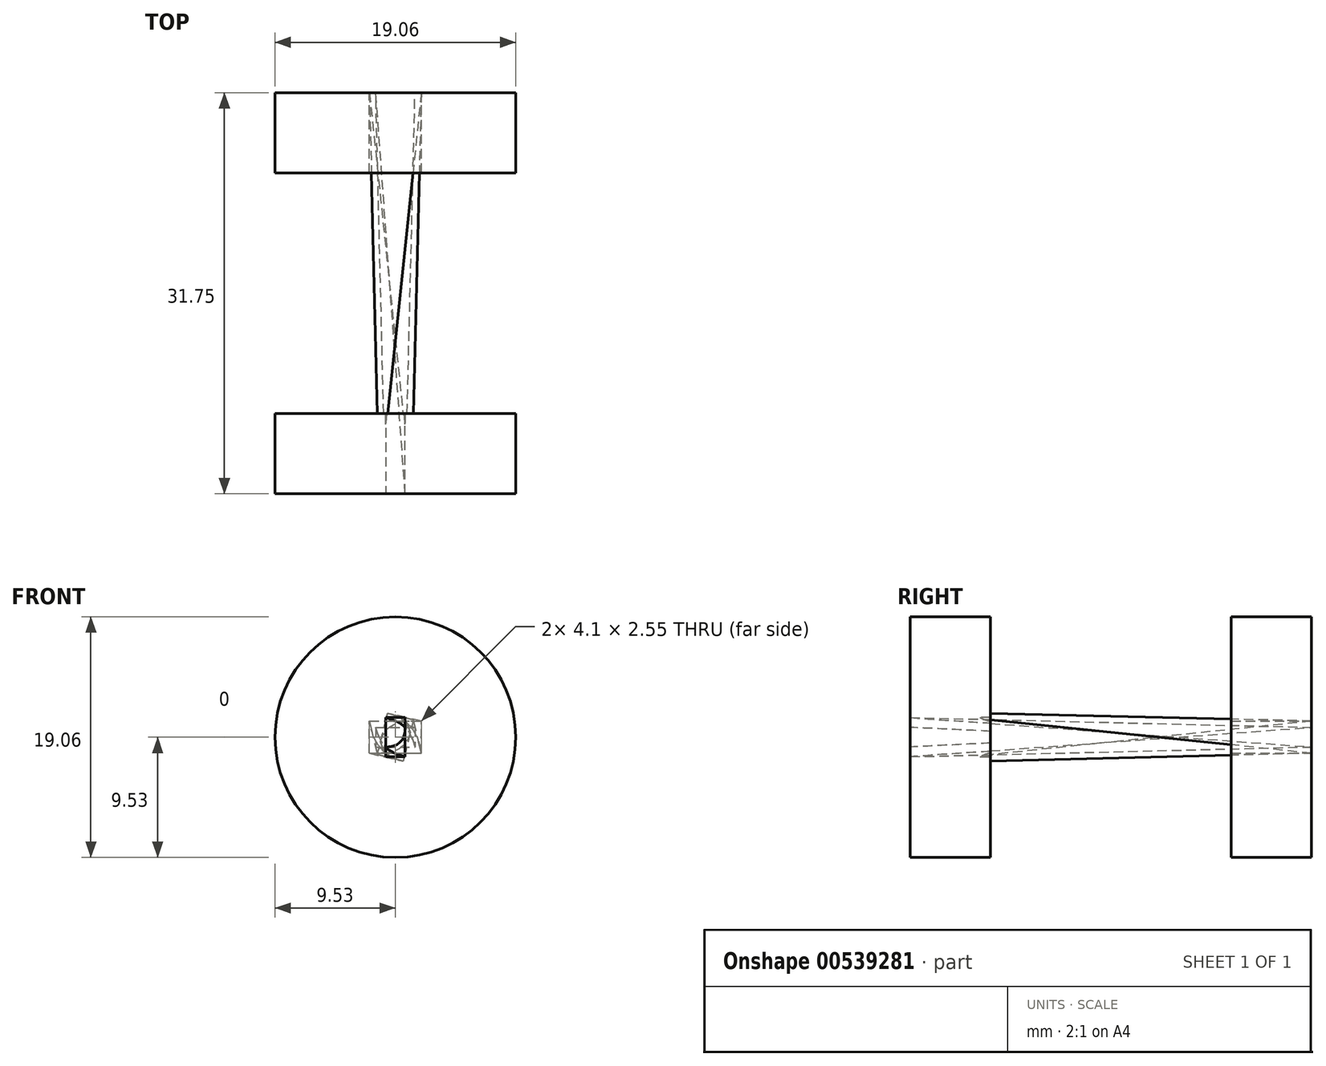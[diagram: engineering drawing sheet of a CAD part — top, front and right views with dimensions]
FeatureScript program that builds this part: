
annotation { "Feature Type Name" : "Feature", "Feature Type Description" : "" }
export const myFeature = defineFeature(function(context is Context, id is Id, definition is map)
    precondition{}
    {
        {
            var Q0;
            Q0=qCreatedBy(makeId("Front.planeOp"),FACE);
            var sketch = newSketch(context, id + "F0", { "sketchPlane" : qUnion([Q0])});
            skPoint(sketch, "E0.middle", {"position": v(0, 0) * mm});
            skLineSegment(sketch, "E1.bottom", {"start": v(-2.05, -1.27) * mm, "end": v(2.05, -1.27) * mm});
            skLineSegment(sketch, "E1.top", {"start": v(-2.05, 1.27) * mm, "end": v(2.05, 1.27) * mm});
            skLineSegment(sketch, "E1.left", {"start": v(-2.05, -1.27) * mm, "end": v(-2.05, 1.27) * mm});
            skLineSegment(sketch, "E1.right", {"start": v(2.05, -1.27) * mm, "end": v(2.05, 1.27) * mm});
            skCircle(sketch, "E2", {"center": v(0, 0) * mm, "radius": 9.53 * mm});
            skSolve(sketch);
        }
        {
            var Q0;
            Q0=qCreatedBy(makeId("Front.planeOp"),FACE);
            cPlane(context, id + "F1", {"entities" : qUnion([Q0]), "cplaneType" : CPlaneType.OFFSET, "offset" : 31.75 * mm, "width" : 150 * mm, "height" : 150 * mm});
        }
        {
            var Q0;
            Q0=qCreatedBy(id+"F1.planeOp",FACE);
            var sketch = newSketch(context, id + "F2", { "sketchPlane" : qUnion([Q0])});
            skLineSegment(sketch, "E3.bottom", {"start": v(-1.27, 2.05) * mm, "end": v(1.28, 2.05) * mm});
            skLineSegment(sketch, "E3.top", {"start": v(-1.28, -2.05) * mm, "end": v(1.27, -2.05) * mm});
            skLineSegment(sketch, "E3.left", {"start": v(-1.27, 2.05) * mm, "end": v(-1.28, -2.05) * mm});
            skLineSegment(sketch, "E3.right", {"start": v(1.28, 2.05) * mm, "end": v(1.27, -2.05) * mm});
            skPoint(sketch, "E3.middle", {"position": v(0, 0) * mm});
            skSolve(sketch);
        }
        {
            var Q0;
            Q0=qCreatedBy(id+"F1.planeOp",FACE);
            var sketch = newSketch(context, id + "F3", { "sketchPlane" : qUnion([Q0])});
            skLineSegment(sketch, "E4.bottom", {"start": v(-0.77, -1.55) * mm, "end": v(0.77, -1.55) * mm});
            skLineSegment(sketch, "E4.top", {"start": v(-0.78, 1.55) * mm, "end": v(0.77, 1.55) * mm});
            skLineSegment(sketch, "E4.left", {"start": v(-0.78, -1.55) * mm, "end": v(-0.78, 1.55) * mm});
            skLineSegment(sketch, "E4.right", {"start": v(0.78, -1.55) * mm, "end": v(0.77, 1.55) * mm});
            skPoint(sketch, "E4.middle", {"position": v(0, 0) * mm});
            skCircle(sketch, "E5", {"center": v(0, 0) * mm, "radius": 9.53 * mm});
            skSolve(sketch);
        }
        {
            var Q0;
            Q0=qCreatedBy(makeId("Front.planeOp"),FACE);
            var sketch = newSketch(context, id + "F4", { "sketchPlane" : qUnion([Q0])});
            skLineSegment(sketch, "E6.bottom", {"start": v(-1.55, 0.78) * mm, "end": v(1.55, 0.78) * mm});
            skLineSegment(sketch, "E6.top", {"start": v(-1.55, -0.78) * mm, "end": v(1.55, -0.78) * mm});
            skLineSegment(sketch, "E6.left", {"start": v(-1.55, 0.78) * mm, "end": v(-1.55, -0.78) * mm});
            skLineSegment(sketch, "E6.right", {"start": v(1.55, 0.78) * mm, "end": v(1.55, -0.78) * mm});
            skPoint(sketch, "E6.middle", {"position": v(0, 0) * mm});
            skSolve(sketch);
        }
        {
            var Q0;
            Q0=makeQuery(id+"F0.imprint","IMPRINT",FACE,{"disambiguationData":[TD([[makeQuery(id+"F0.imprint","IMPRINT",EDGE,{"derivedFrom":sQuery(id+"F0.wireOp",EDGE,"E1.bottom")}),-1.0]])]});
            extrude(context, id + "F5", {"entities" : qUnion([Q0]), "depth" : 6.35 * mm, "offsetDistance" : 25 * mm});
        }
        {
            var Q0;
            Q0=makeQuery(id+"F0.imprint","IMPRINT",FACE,{"disambiguationData":[TD([[makeQuery(id+"F0.imprint","IMPRINT",EDGE,{"derivedFrom":sQuery(id+"F0.wireOp",EDGE,"E1.bottom")}),1.0]])]});
            var Q1;
            Q1 = qSketchRegion(id + "F2", true);
            var Q2;
            Q2=sQuery(id+"F2.wireOp",VERTEX,"E3.right.start");
            var Q3;
            Q3=sQuery(id+"F0.wireOp",VERTEX,"E1.right.start");
            loft(context, id + "F6", {"sheetProfilesArray" : [{ "sheetProfileEntities" : qUnion([Q0]) }, { "sheetProfileEntities" : qUnion([Q1]) }], "matchConnections" : true, "connections" : [{ "connectionEntities" : qUnion([Q2, Q3]), "connectionEdgeQueries" : qUnion([]), "connectionEdgeParameters" : [] }]});
        }
        {
            var Q0;
            Q0=makeQuery(id+"F3.imprint","IMPRINT",FACE,{"disambiguationData":[TD([[makeQuery(id+"F3.imprint","IMPRINT",EDGE,{"derivedFrom":sQuery(id+"F3.wireOp",EDGE,"E4.bottom")}),1.0]])]});
            var Q1;
            Q1=makeQuery(id+"F4.imprint","IMPRINT",FACE,{"disambiguationData":[TD([[makeQuery(id+"F4.imprint","IMPRINT",EDGE,{"derivedFrom":sQuery(id+"F4.wireOp",EDGE,"E6.bottom")}),-1.0]])]});
            var Q2;
            Q2=sQuery(id+"F4.wireOp",VERTEX,"E6.left.start");
            var Q3;
            Q3=sQuery(id+"F3.wireOp",VERTEX,"E4.left.start");
            loft(context, id + "F7", {"operationType" : NewBodyOperationType.REMOVE, "sheetProfilesArray" : [{ "sheetProfileEntities" : qUnion([Q0]) }, { "sheetProfileEntities" : qUnion([Q1]) }], "matchConnections" : true, "connections" : [{ "connectionEntities" : qUnion([Q2, Q3]), "connectionEdgeQueries" : qUnion([]), "connectionEdgeParameters" : [] }]});
        }
        {
            var Q0;
            Q0 = qSketchRegion(id + "F3", true);
            extrude(context, id + "F8", {"entities" : qUnion([Q0]), "operationType" : NewBodyOperationType.ADD, "oppositeDirection" : true, "depth" : 6.35 * mm, "offsetDistance" : 25 * mm});
        }
    });
